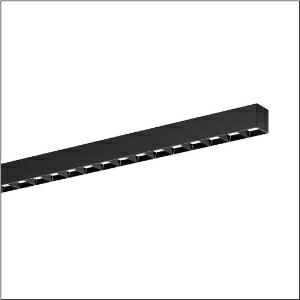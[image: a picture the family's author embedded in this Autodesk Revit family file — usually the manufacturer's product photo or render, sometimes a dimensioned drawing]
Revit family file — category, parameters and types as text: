
# Revit family: silica_r__21_51mx24dc4abb_c2b6
name_source: partatom
category: Lighting Fixtures
units: mm (PartAtom-declared; Revit-internal decimal feet)

## family parameters
Cut with Voids When Loaded = No
Host = Face
Light Source = No
Part Type = Normal
Room Calculation Point = No
Round Connector Dimension = Use Diameter
Shared = No

## types (1)
- --- (1 x LED, 10800 lm, 73.7 W, 4000K)
    Apparent Load = 74 VA
    CIE Flux Codes = 74 94 99 100 100
    Color Rendering = 80
    Color Temperature = 4000K
    Default Elevation = 1800 mm
    Description = Silica® 21, office luminaire, primary light control with darklight reflector, of PMMA, black, CAT 2 (L<= 3000cd/m²), light emission: direct distribution, primary light characteristic: asymmetric, installation type: surface-mounted, LED, rated luminous flux: 10.800lm, luminous efficacy: 147lm/W, light colour: 840, colour temperature: 4000K, with terminal, 3+2-pole, max. 2.5mm², mains connection: 220..240V, AC, 50/60Hz, rated input power: 73.7W, luminaire housing, of aluminium, jet black (RAL 9005), length: 3.004mm, width: 53mm, height: 53mm, protection rating (complete): IP20, insulation class (complete): insulation class I (protective earthing), certification: CE, permissible operating ambient temperature: 0..+35°C, standard: EN 50419, packaging unit: 1 piece
    Height = 0 mm  [stored 0 ft]
    Lamp = 1 x LED
    Lamp Light Flux = 10800 lm
    Lamp Power = 73.7 W
    Lamp count = 1
    Length = 3004 mm
    Luminous efficacy = 147 lm/W
    Manufacturer = Siteco
    ModVariant = No
    Model = 51MX24DC4ABB
    Mounting Place = Ceiling
    Mounting Type = Recessed
    Number of Poles = 1
    OnlyDefault = Yes
    Power Factor = 1
    Product Name = Silica® 21
    Product group = office luminaire | ceiling recessed
    ProductGroupID = 401
    Protection Class = Protection class I
    Protection Degree = IP 20
    RLX_Detail_Level = 1
    RLX_Emergency_Light_Flux = 0 lm
    RLX_Emergency_Type = 0
    RLX_Emergency_Type_DB = No
    RlxData = <blob elided: 64569 chars, md5=f27cd37c>
    Socket = socket
    Standby Power = 0 W
    System Light Flux = 10800 lm
    System Power = 74 W
    Type Comments = factory setting: luminous flux: 100 % | dim-lin: 254 | 418 mA
    Type Image = l_1297756.jpg
    URL = http://relux.com
    VarID = @adj_053561
    Voltage = 0 V
    Weight = 0.00 kg
    Width = 53 mm

note: [stored X ft] marks values corroborated as IEEE doubles in the binary element streams (Revit-internal decimal feet)

## geometry (parser evidence)
native form markers: Blend x4, Sweep x11
no freeform markers — native parametric forms only
